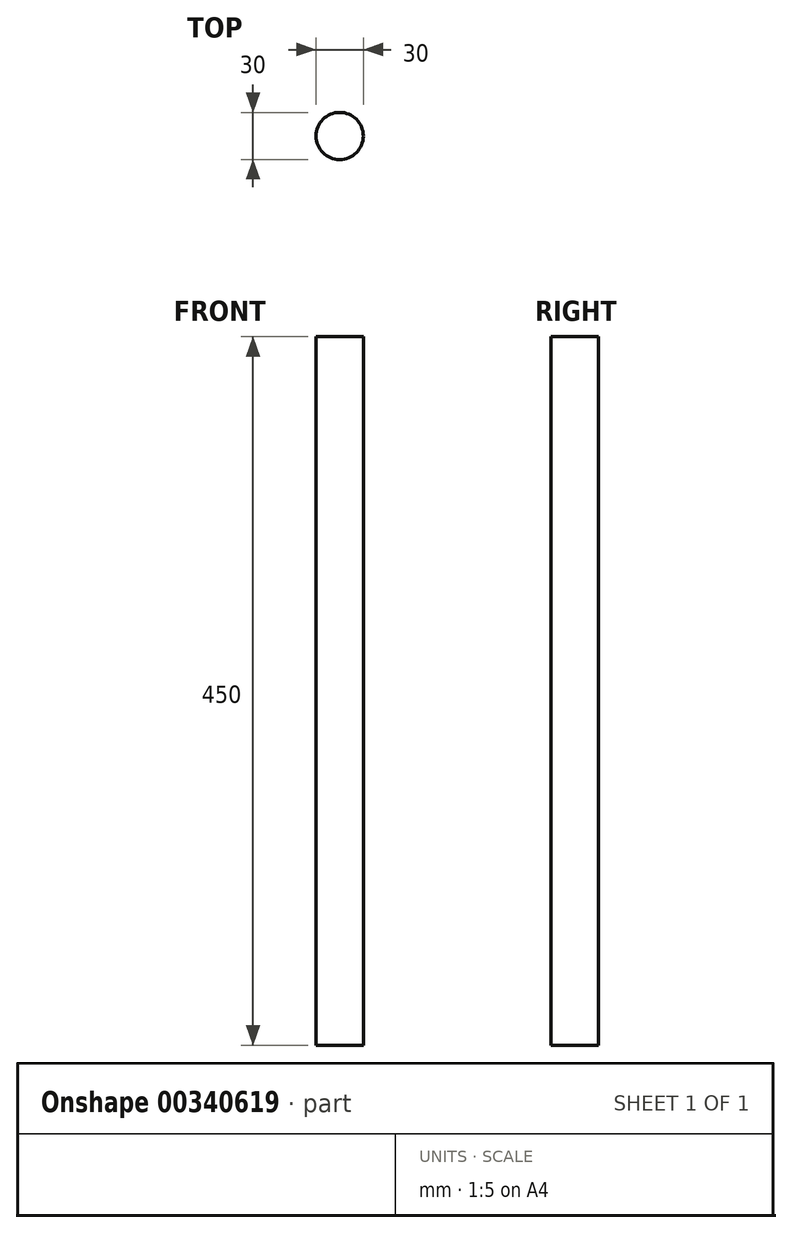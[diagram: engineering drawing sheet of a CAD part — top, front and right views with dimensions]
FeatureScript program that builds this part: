
annotation { "Feature Type Name" : "Feature", "Feature Type Description" : "" }
export const myFeature = defineFeature(function(context is Context, id is Id, definition is map)
    precondition{}
    {
        {
            var Q0;
            Q0=qCreatedBy(makeId("Top.planeOp"),FACE);
            var sketch = newSketch(context, id + "F0", { "sketchPlane" : qUnion([Q0])});
            skCircle(sketch, "E0", {"center": v(0, 0) * mm, "radius": 15 * mm});
            skSolve(sketch);
        }
        {
            var Q0;
            Q0 = qSketchRegion(id + "F0", true);
            extrude(context, id + "F1", {"entities" : qUnion([Q0]), "depth" : 450 * mm});
        }
    });
